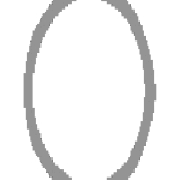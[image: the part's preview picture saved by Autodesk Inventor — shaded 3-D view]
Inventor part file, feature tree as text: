
AUTODESK INVENTOR PART (.ipt)
format: ipt  version: 2021 (Build 250183000, 183)  size: 111,616 bytes
history: native  units: in
note: dims shown in document units (in); Inventor stores cm internally (conversion verified against a paired STEP export)
features: other x4, sketch x3, plane x1
ambient origin geometry x8: Origin, YZ Plane, XZ Plane, XY Plane, X Axis, Y Axis, Z Axis, Center Point
bodies: Solid1 (feature_tree), Body (feature_tree)
feature tree (8):
  other  "Driven Length"
  other  "Frame Generator"
  other  "Start Plane"
  other  "End Plane"
  sketch  "Sketch"  dims[d2=5.831in d4=-0.0in d5=5.831in d6=0.12in d7=0.0in d8=90.0deg d9=5.831in]
  sketch  "Sketch2"  dims[d0=1.0in]
  plane  "Work Plane3"
  sketch  "Sketch3"  dims[d1=0.065in]
